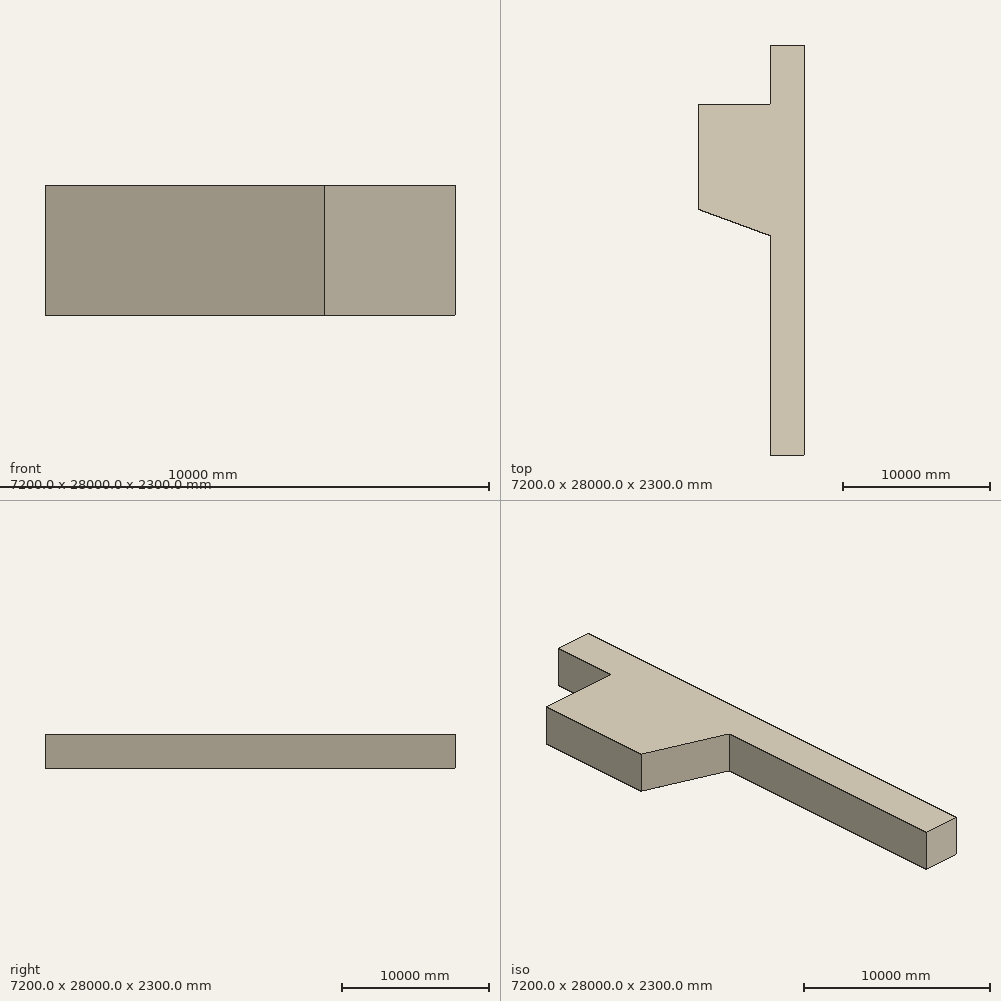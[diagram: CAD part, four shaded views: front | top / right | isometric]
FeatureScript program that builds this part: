
annotation { "Feature Type Name" : "Feature", "Feature Type Description" : "" }
export const myFeature = defineFeature(function(context is Context, id is Id, definition is map)
    precondition{}
    {
        {
            var Q0;
            Q0=qCreatedBy(makeId("Top.planeOp"),FACE);
            var sketch = newSketch(context, id + "F0", { "sketchPlane" : qUnion([Q0])});
            skLineSegment(sketch, "E0", {"start": v(7200, 4000) * mm, "end": v(4900, 4000) * mm});
            skLineSegment(sketch, "E1", {"start": v(4900, 4000) * mm, "end": v(4900, 0) * mm});
            skLineSegment(sketch, "E2", {"start": v(4900, 0) * mm, "end": v(0, 0) * mm});
            skLineSegment(sketch, "E3", {"start": v(0, 0) * mm, "end": v(0, -7200) * mm});
            skLineSegment(sketch, "E4", {"start": v(0, -7200) * mm, "end": v(4900, -9000) * mm});
            skLineSegment(sketch, "E5", {"start": v(4900, -9000) * mm, "end": v(7200, -9000) * mm});
            skLineSegment(sketch, "E6", {"start": v(7200, -9000) * mm, "end": v(7200, 4000) * mm});
            skLineSegment(sketch, "E7", {"start": v(4900, -9000) * mm, "end": v(4900, -24000) * mm});
            skLineSegment(sketch, "E8", {"start": v(4900, -24000) * mm, "end": v(7200, -24000) * mm});
            skLineSegment(sketch, "E9", {"start": v(7200, -24000) * mm, "end": v(7200, -9000) * mm});
            skSolve(sketch);
        }
        {
            var Q0;
            Q0=makeQuery(id+"F0.imprint","IMPRINT",FACE,{"disambiguationData":[TD([[makeQuery(id+"F0.imprint","IMPRINT",EDGE,{"derivedFrom":sQuery(id+"F0.wireOp",EDGE,"E0")}),1.0]])]});
            var Q1;
            Q1=makeQuery(id+"F0.imprint","IMPRINT",FACE,{"disambiguationData":[TD([[makeQuery(id+"F0.imprint","IMPRINT",EDGE,{"derivedFrom":sQuery(id+"F0.wireOp",EDGE,"E5")}),-1.0]])]});
            extrude(context, id + "F1", {"entities" : qUnion([Q0, Q1]), "depth" : 2300 * mm, "offsetDistance" : 25 * mm});
        }
    });
